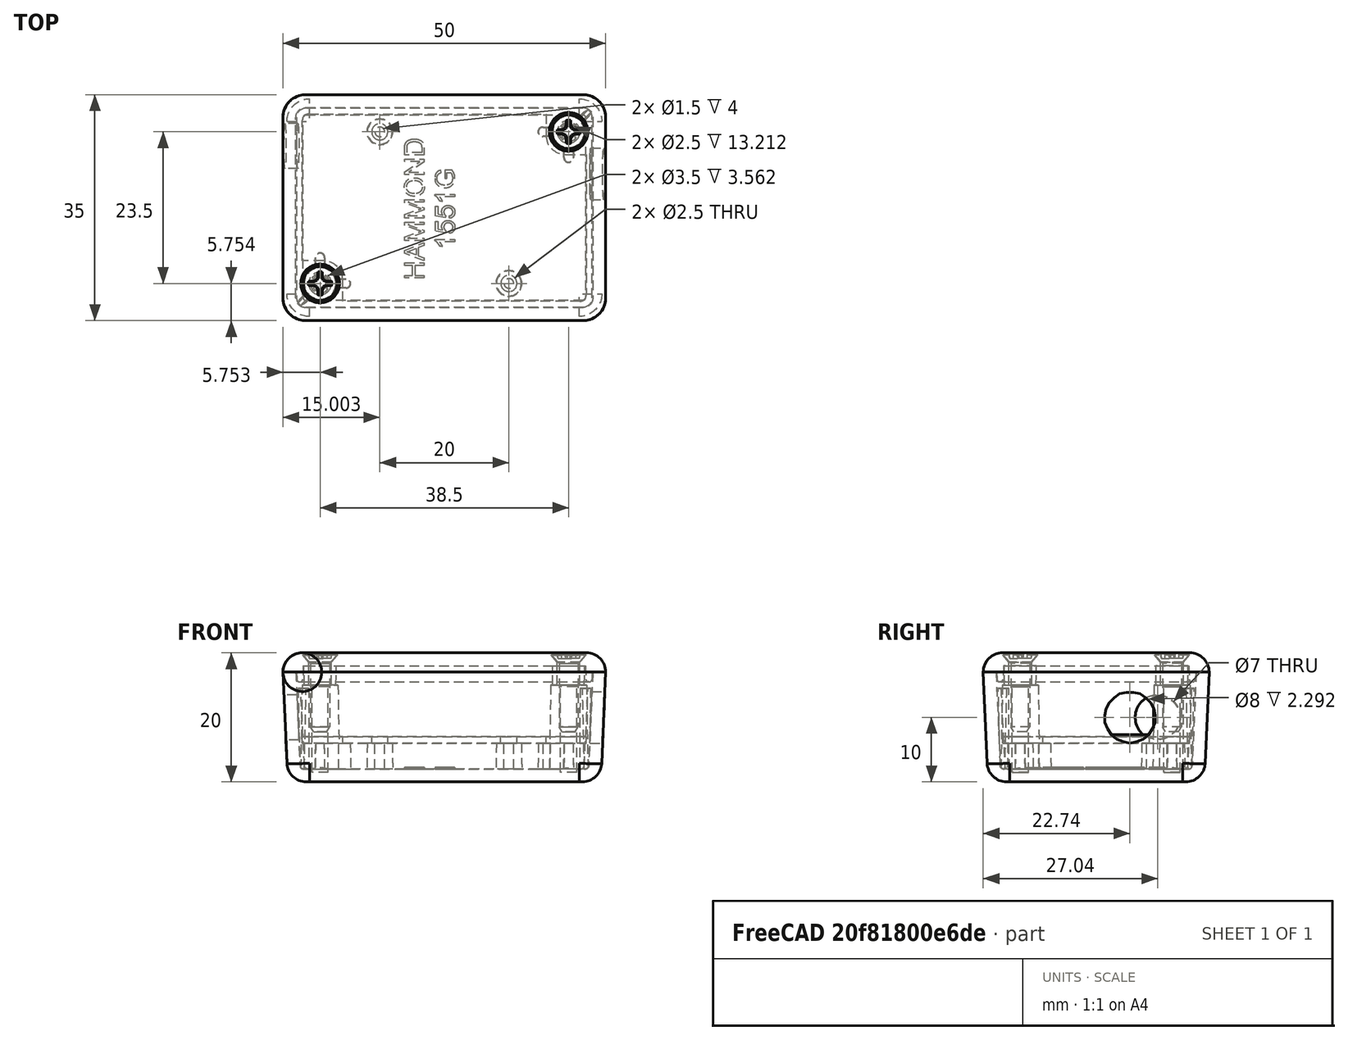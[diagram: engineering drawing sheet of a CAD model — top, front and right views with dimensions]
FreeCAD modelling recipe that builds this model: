
FCSTD DOCUMENT  (FreeCAD 0.16R6712 (Git))
Label: Pt100
License: All rights reserved
LicenseURL: http://en.wikipedia.org/wiki/All_rights_reserved
objects: Part::Feature×5, Part::Cylinder×2, App::VRMLObject×1, Part::MultiFuse×1, Part::Cut×1
note: 9 computed .brp shape members not serialized (recipe doc carries the construction recipe); baked Part::Feature solids carry a one-line shape summary decoded from their .brp

FEATURE [Part::Feature] Part__Feature  label="1551G Box"
  shape: bbox 50.01 x 35.01 x 126.7 mm, 244 faces (baked)
FEATURE [Part::Feature] Part__Feature001  label="1551F-G Lid"
  Placement = pos=(-10.5769,-2.53606,3) rot=(0,1,0;3.14159rad)
  shape: bbox 50 x 35 x 5 mm, 54 faces (baked)
FEATURE [Part::Feature] Part__Feature002  label="1551G PCB"
  Placement = pos=(-10.5769,-2.53606,-11) rot=(0,0,1;0rad)
  shape: bbox 44 x 29 x 1 mm, 16 faces (baked)
FEATURE [Part::Feature] Part__Feature003  label="SC510 (screw #4X 1_2' FH)"
  Placement = pos=(-29.8269,-14.2861,1.33113) rot=(1,0,0;1.5708rad)
  shape: bbox 5.232 x 5.232 x 12.12 mm, 27 faces (baked)
FEATURE [Part::Feature] Part__Feature004  label="SC510 (screw #4X 1_2' FH)001"
  Placement = pos=(8.67308,9.21394,1.33113) rot=(1,0,0;1.5708rad)
  shape: bbox 5.232 x 5.232 x 12.12 mm, 27 faces (baked)
FEATURE [App::VRMLObject] Pt100
  Placement = pos=(20.9,-118,-10.2) rot=(0,0,1;0rad)
FEATURE [Part::Cylinder] Cylinder
  Angle = 360
  Height = 3
  Placement = pos=(12,2.7,-7) rot=(0,1,0;1.5708rad)
  Radius = 4
FEATURE [Part::Cylinder] Cylinder001
  Angle = 360
  Height = 3
  Placement = pos=(-33,7,-7) rot=(0,-1,0;1.5708rad)
  Radius = 3.5
FEATURE [Part::MultiFuse] Fusion
  Shapes = -> [Cylinder001,Cylinder]
FEATURE [Part::Cut] Cut
  Base = -> Part__Feature
  Tool = -> Fusion
